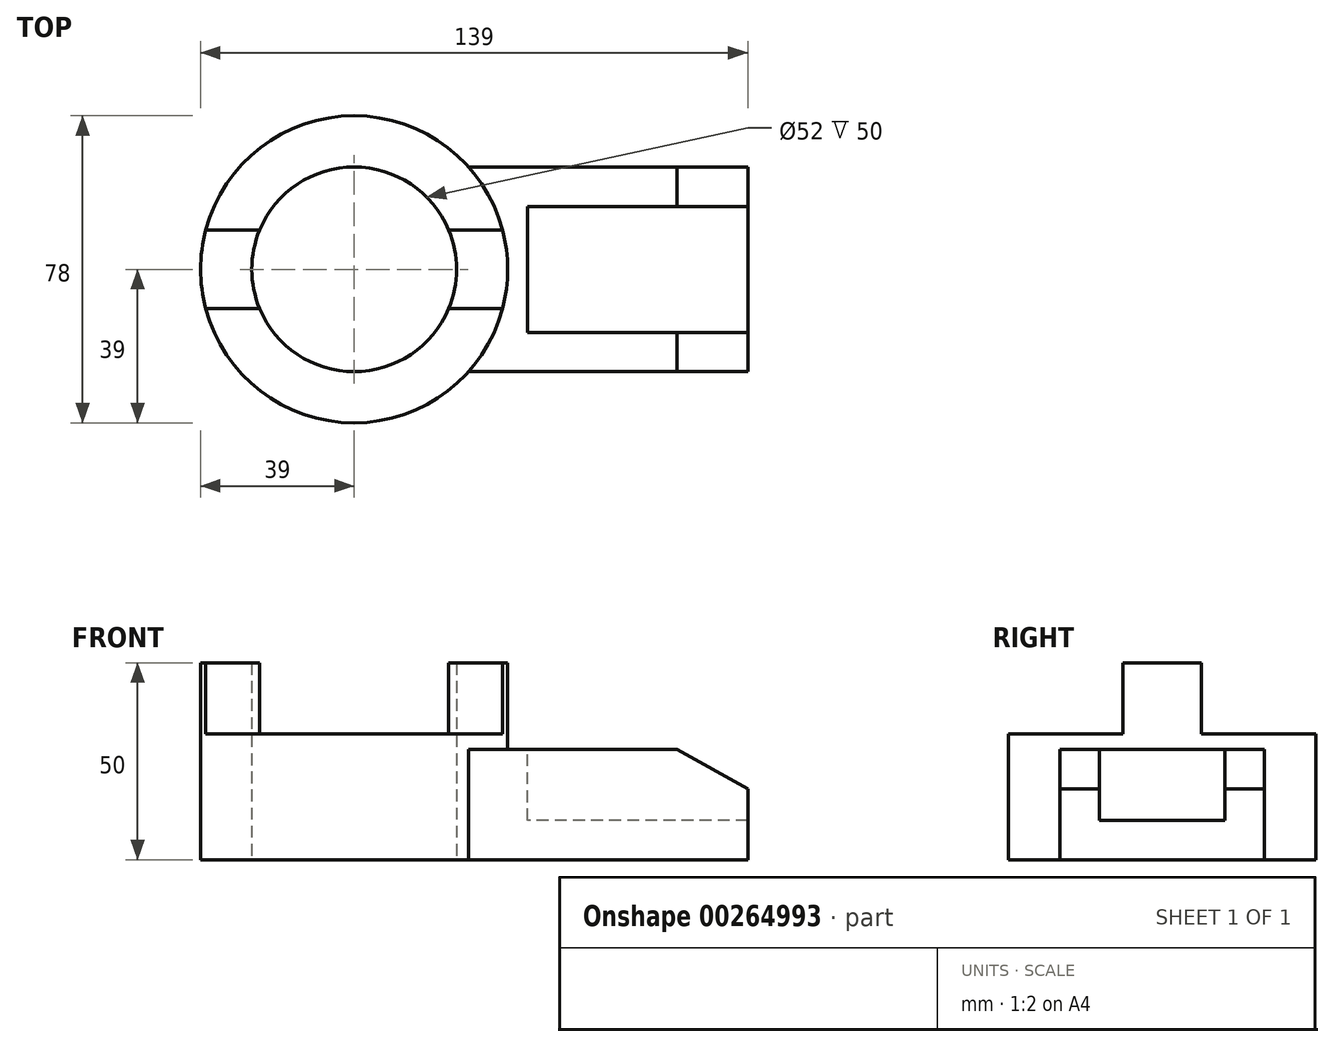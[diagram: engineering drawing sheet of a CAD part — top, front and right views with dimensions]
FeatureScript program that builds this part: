
annotation { "Feature Type Name" : "Feature", "Feature Type Description" : "" }
export const myFeature = defineFeature(function(context is Context, id is Id, definition is map)
    precondition{}
    {
        {
            var Q0;
            Q0=qCreatedBy(makeId("Top.planeOp"),FACE);
            var sketch = newSketch(context, id + "F0", { "sketchPlane" : qUnion([Q0])});
            skCircle(sketch, "E0", {"center": v(0, 0) * mm, "radius": 26 * mm});
            skCircle(sketch, "E1", {"center": v(0, 0) * mm, "radius": 39 * mm});
            skSolve(sketch);
        }
        {
            var Q0;
            Q0 = qSketchRegion(id + "F0", true);
            extrude(context, id + "F1", {"entities" : qUnion([Q0]), "depth" : 32 * mm});
        }
        {
            var Q0;
            Q0=makeQuery(id+"F1.opExtrude","CAP_FACE",FACE,{"disambiguationData":[OSD([sQuery(id+"F0.wireOp",EDGE,"E0"),sQuery(id+"F0.wireOp",EDGE,"E1")])],"isStart":false});
            var sketch = newSketch(context, id + "F2", { "sketchPlane" : qUnion([Q0])});
            skLineSegment(sketch, "E2", {"start": v(-37.7, -10) * mm, "end": v(-24, -10) * mm});
            skLineSegment(sketch, "E3", {"start": v(-24, 10) * mm, "end": v(-37.7, 10) * mm});
            skArc(sketch, "E4", {"start": v(-37.7, 10) * mm, "mid": v(-39, 0) * mm, "end": v(-37.7, -10) * mm});
            skArc(sketch, "E5", {"start": v(-24, 10) * mm, "mid": v(-26, 0) * mm, "end": v(-24, -10) * mm});
            skLineSegment(sketch, "E6.MirrorCS", {"start": v(24, 10) * mm, "end": v(37.7, 10) * mm});
            skArc(sketch, "E7.MirrorCS", {"start": v(37.7, 10) * mm, "mid": v(39, 0) * mm, "end": v(37.7, -10) * mm});
            skLineSegment(sketch, "E8.MirrorCS", {"start": v(37.7, -10) * mm, "end": v(24, -10) * mm});
            skArc(sketch, "E9.MirrorCS", {"start": v(24, 10) * mm, "mid": v(26, 0) * mm, "end": v(24, -10) * mm});
            skSolve(sketch);
        }
        {
            var Q0;
            Q0 = qSketchRegion(id + "F2", true);
            extrude(context, id + "F3", {"entities" : qUnion([Q0]), "operationType" : NewBodyOperationType.ADD, "depth" : 18 * mm});
        }
        {
            var Q0;
            Q0=qCreatedBy(makeId("Top.planeOp"),FACE);
            var sketch = newSketch(context, id + "F4", { "sketchPlane" : qUnion([Q0])});
            skArc(sketch, "E10", {"start": v(29.07, -26) * mm, "mid": v(39, 0) * mm, "end": v(29.07, 26) * mm});
            skLineSegment(sketch, "E11", {"start": v(29.07, -26) * mm, "end": v(100, -26) * mm});
            skLineSegment(sketch, "E12", {"start": v(29.07, 26) * mm, "end": v(100, 26) * mm});
            skLineSegment(sketch, "E13", {"start": v(100, 26) * mm, "end": v(100, -26) * mm});
            skSolve(sketch);
        }
        {
            var Q0;
            Q0 = qSketchRegion(id + "F4", true);
            extrude(context, id + "F5", {"entities" : qUnion([Q0]), "operationType" : NewBodyOperationType.ADD, "depth" : 28 * mm});
        }
        {
            var Q0;
            Q0=makeQuery(id+"F5.opExtrude","CAP_FACE",FACE,{"disambiguationData":[OSD([sQuery(id+"F4.wireOp",EDGE,"E10"),sQuery(id+"F4.wireOp",EDGE,"E11"),sQuery(id+"F4.wireOp",EDGE,"E12"),sQuery(id+"F4.wireOp",EDGE,"E13")])],"isStart":false});
            var sketch = newSketch(context, id + "F6", { "sketchPlane" : qUnion([Q0])});
            skLineSegment(sketch, "E14.bottom", {"start": v(100, 16) * mm, "end": v(44, 16) * mm});
            skLineSegment(sketch, "E14.top", {"start": v(100, -16) * mm, "end": v(44, -16) * mm});
            skLineSegment(sketch, "E14.left", {"start": v(100, 16) * mm, "end": v(100, -16) * mm});
            skLineSegment(sketch, "E14.right", {"start": v(44, 16) * mm, "end": v(44, -16) * mm});
            skSolve(sketch);
        }
        {
            var Q0;
            Q0 = qSketchRegion(id + "F6", true);
            extrude(context, id + "F7", {"entities" : qUnion([Q0]), "operationType" : NewBodyOperationType.REMOVE, "oppositeDirection" : true, "depth" : 18 * mm});
        }
        {
            var Q0;
            {var subQ0=sQuery(id+"F4.wireOp",EDGE,"E13");var subQ1=sQuery(id+"F4.wireOp",EDGE,"E11");Q0=makeQuery(id+"F7.boolean.opBoolean","SPLIT",EDGE,{"disambiguationData":[TD([makeQuery(id+"F5.opExtrude","SWEPT_FACE",FACE,{"disambiguationData":[OSD([subQ1])]})])],"derivedFrom":makeQuery(id+"F5.opExtrude","CAP_EDGE",EDGE,{"disambiguationData":[OSD([subQ0])],"isStart":false})});}
            var Q1;
            {var subQ0=sQuery(id+"F4.wireOp",EDGE,"E13");var subQ1=sQuery(id+"F4.wireOp",EDGE,"E12");Q1=makeQuery(id+"F7.boolean.opBoolean","SPLIT",EDGE,{"disambiguationData":[TD([makeQuery(id+"F5.opExtrude","SWEPT_FACE",FACE,{"disambiguationData":[OSD([subQ1])]})])],"derivedFrom":makeQuery(id+"F5.opExtrude","CAP_EDGE",EDGE,{"disambiguationData":[OSD([subQ0])],"isStart":false})});}
            chamfer(context, id + "F8", {"entities" : qUnion([Q0, Q1]), "chamferType" : ChamferType.TWO_OFFSETS, "width1" : 10 * mm, "oppositeDirection" : false, "width2" : 18 * mm, "tangentPropagation" : true});
        }
    });
